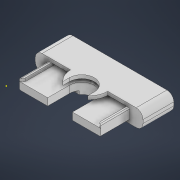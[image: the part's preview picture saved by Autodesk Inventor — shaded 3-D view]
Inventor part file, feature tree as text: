
AUTODESK INVENTOR PART (.ipt)
format: ipt  version: 2022 (Build 260153000, 153)  size: 517,632 bytes
history: native  units: mm
features: sketch x14, extrude x11, fillet x4, emboss x1
ambient origin geometry x8: Origin, YZ Plane, XZ Plane, XY Plane, X Axis, Y Axis, Z Axis, Center Point
bodies: Body1 (feature_tree)
feature tree (30):
  extrude  "Extrusion8"  Depth=10.0mm
  extrude  "Extrusion9"  Depth=35.0mm
  extrude  "Extrusion10"  Depth=35.0mm TaperAngle=0.0deg
  extrude  "Extrusion11"  Depth=17.0mm
  extrude  "Extrusion12"  Depth=2.0mm TaperAngle=0.0deg
  fillet  "Fillet5"  Radius=33.0mm
  extrude  "Extrusion13"  Depth=17.0mm
  fillet  "Fillet6"  Radius=17.0mm
  emboss  "Emboss3"
  sketch  "Sketch22"  dims[d64=0.2mm d65=0.0mm d66=0.2mm d67=0.0mm]
  extrude  "Extrusion14"  Depth=1.0mm TaperAngle=0.0deg
  extrude  "Extrusion16"  Depth=0.2mm TaperAngle=0.0deg
  extrude  "Extrusion15"  Depth=4.0mm
  fillet  "Fillet7"  Radius=63.0mm
  sketch  "Sketch25"  dims[d75=3.8mm d76=0.0mm d77=20.0mm d78=0.0mm]
  extrude  "Extrusion17"  Depth=17.0mm
  fillet  "Fillet8"  Radius=7.25mm
  extrude  "Extrusion18"  Depth=3.8mm TaperAngle=0.0deg
  sketch  "Sketch13"  dims[d38=63.0mm d39=10.0mm]
  sketch  "Sketch15"  dims[d40=35.0mm d41=0.0mm d42=12.75mm]
  sketch  "Sketch16"  dims[d43=14.5mm d44=35.0mm d45=0.0mm]
  sketch  "Sketch17"  dims[d46=63.0mm d47=17.0mm]
  sketch  "Sketch19"  dims[d48=2.0mm d49=0.0mm d51=2.0mm d52=0.0mm d55=33.0mm d56=0.0mm]
  sketch  "Sketch20"  dims[d57=2.0mm d58=48.0mm d59=17.0mm d60=0.0mm]
  sketch  "Sketch21"  dims[d61=1.0mm d62=1.0mm d63=0.0mm]
  sketch  "Sketch23"  dims[d68=1.8mm d69=4.0mm d71=63.0mm]
  sketch  "Sketch24"  dims[d72=17.0mm d73=17.0mm d74=7.25mm]
  sketch  "Sketch26"  dims[d79=0.3mm]
  sketch  "Sketch27"  dims[d80=21.7mm]
  sketch  "Sketch28"  dims[d81=2.0mm d82=0.0mm]
